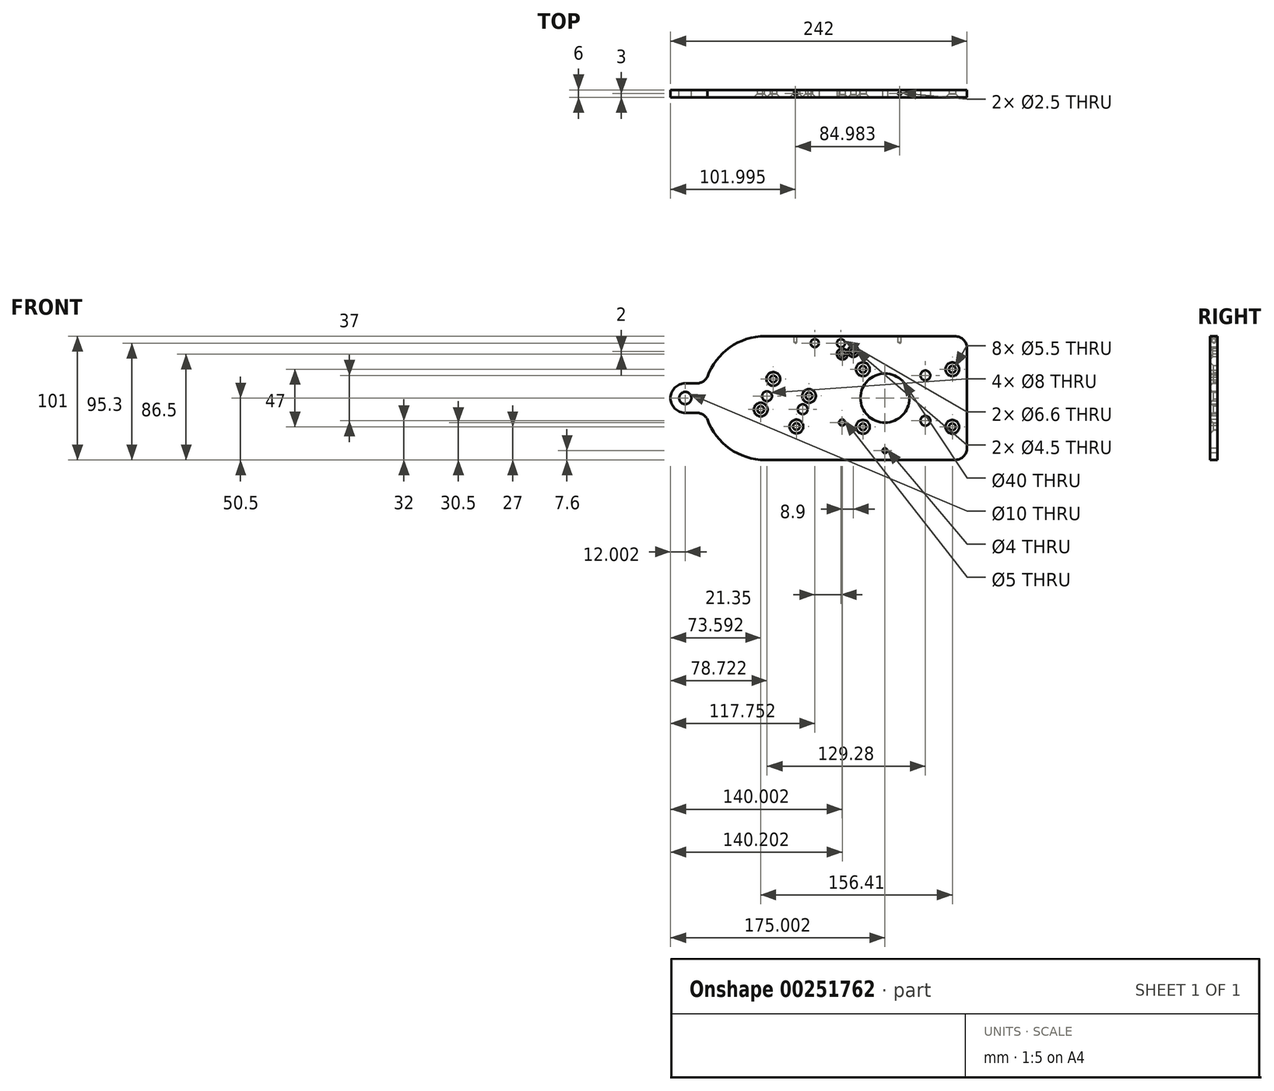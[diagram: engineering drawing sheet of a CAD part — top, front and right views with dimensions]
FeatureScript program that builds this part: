
annotation { "Feature Type Name" : "Feature", "Feature Type Description" : "" }
export const myFeature = defineFeature(function(context is Context, id is Id, definition is map)
    precondition{}
    {
        {
            var Q0;
            Q0=qCreatedBy(makeId("Front.planeOp"),FACE);
            var sketch = newSketch(context, id + "F0", { "sketchPlane" : qUnion([Q0])});
            skCircle(sketch, "E0", {"center": v(37.1, 0) * mm, "radius": 20 * mm});
            skCircle(sketch, "E1", {"center": v(-125.9, 0) * mm, "radius": 5 * mm});
            skArc(sketch, "E2", {"start": v(-125.9, 12) * mm, "mid": v(-137.9, 0) * mm, "end": v(-125.9, -12) * mm});
            skLineSegment(sketch, "E3", {"start": v(-125.9, 12) * mm, "end": v(-116.7, 12) * mm});
            skLineSegment(sketch, "E4", {"start": v(-60.79, 50.5) * mm, "end": v(94.1, 50.5) * mm});
            skLineSegment(sketch, "E5", {"start": v(104.1, 40.5) * mm, "end": v(104.1, -40.5) * mm});
            skLineSegment(sketch, "E6", {"start": v(94.1, -50.5) * mm, "end": v(-29.62, -50.5) * mm});
            skLineSegment(sketch, "E7", {"start": v(-125.9, -12) * mm, "end": v(-116.7, -12) * mm});
            skPoint(sketch, "E8.MirrorCS.start.orphan", {"position": v(-116.7, -12) * mm});
            skPoint(sketch, "E9.visualSharp", {"position": v(-29.62, 50.5) * mm});
            skArc(sketch, "E9.filletArc", {"start": v(-60.79, 50.5) * mm, "mid": v(-60.84, 50.5) * mm, "end": v(-60.89, 50.47) * mm});
            skPoint(sketch, "E10.MirrorCS.end.orphan", {"position": v(-29.62, -50.5) * mm});
            skArc(sketch, "E11", {"start": v(-116.7, 12) * mm, "mid": v(-111.58, 13.41) * mm, "end": v(-107.9, 17.25) * mm});
            skArc(sketch, "E12", {"start": v(-60.79, 50.5) * mm, "mid": v(-89.62, 41.35) * mm, "end": v(-107.9, 17.25) * mm});
            skArc(sketch, "E13.MirrorCS", {"start": v(-116.7, -12) * mm, "mid": v(-111.58, -13.41) * mm, "end": v(-107.9, -17.25) * mm});
            skArc(sketch, "E14.MirrorCS", {"start": v(-60.79, -50.5) * mm, "mid": v(-89.62, -41.35) * mm, "end": v(-107.9, -17.25) * mm});
            skLineSegment(sketch, "E15.MirrorCS", {"start": v(-60.79, -50.5) * mm, "end": v(94.1, -50.5) * mm});
            skPoint(sketch, "E16.visualSharp", {"position": v(104.1, 50.5) * mm});
            skArc(sketch, "E16.filletArc", {"start": v(104.1, 40.5) * mm, "mid": v(101.17, 47.57) * mm, "end": v(94.1, 50.5) * mm});
            skPoint(sketch, "E17.visualSharp", {"position": v(104.1, -50.5) * mm});
            skArc(sketch, "E17.filletArc", {"start": v(94.1, -50.5) * mm, "mid": v(101.17, -47.57) * mm, "end": v(104.1, -40.5) * mm});
            skSolve(sketch);
        }
        {
            var Q0;
            Q0 = qSketchRegion(id + "F0", true);
            extrude(context, id + "F1", {"entities" : qUnion([Q0]), "depth" : 6 * mm});
        }
        {
            var Q0;
            Q0=makeQuery(id+"F1.opExtrude","CAP_FACE",FACE,{"disambiguationData":[OSD([sQuery(id+"F0.wireOp",EDGE,"E0"),sQuery(id+"F0.wireOp",EDGE,"E1"),sQuery(id+"F0.wireOp",EDGE,"E2"),sQuery(id+"F0.wireOp",EDGE,"E3"),sQuery(id+"F0.wireOp",EDGE,"E4"),sQuery(id+"F0.wireOp",EDGE,"E5"),sQuery(id+"F0.wireOp",EDGE,"E7"),sQuery(id+"F0.wireOp",EDGE,"E11"),sQuery(id+"F0.wireOp",EDGE,"E12"),sQuery(id+"F0.wireOp",EDGE,"E13.MirrorCS"),sQuery(id+"F0.wireOp",EDGE,"E14.MirrorCS"),sQuery(id+"F0.wireOp",EDGE,"E15.MirrorCS"),sQuery(id+"F0.wireOp",EDGE,"E16.filletArc"),sQuery(id+"F0.wireOp",EDGE,"E17.filletArc")])],"isStart":false});
            var sketch = newSketch(context, id + "F2", { "sketchPlane" : qUnion([Q0])});
            skPoint(sketch, "E18", {"position": v(-54.05, 15.6) * mm});
            skPoint(sketch, "E19", {"position": v(-64.3, -9.35) * mm});
            skPoint(sketch, "E20", {"position": v(-24.92, 1.75) * mm});
            skPoint(sketch, "E21", {"position": v(-30.05, -9.1) * mm});
            skPoint(sketch, "E22", {"position": v(-35.18, -23.2) * mm});
            skPoint(sketch, "E23", {"position": v(-20.15, 44.8) * mm});
            skPoint(sketch, "E24", {"position": v(1.2, 44.8) * mm});
            skPoint(sketch, "E25", {"position": v(2.3, 36) * mm});
            skPoint(sketch, "E26", {"position": v(11.2, 38) * mm});
            skPoint(sketch, "E27", {"position": v(19.1, 23.5) * mm});
            skPoint(sketch, "E28", {"position": v(19.1, -23.5) * mm});
            skPoint(sketch, "E29", {"position": v(2.1, -20) * mm});
            skPoint(sketch, "E30", {"position": v(37.1, -42.9) * mm});
            skPoint(sketch, "E31", {"position": v(70.1, 18.5) * mm});
            skPoint(sketch, "E32", {"position": v(70.1, -18.5) * mm});
            skPoint(sketch, "E33", {"position": v(37.1, 0) * mm});
            skPoint(sketch, "E34", {"position": v(92.1, 23.5) * mm});
            skPoint(sketch, "E35", {"position": v(92.1, -23.5) * mm});
            skPoint(sketch, "E36", {"position": v(-59.18, 1.52) * mm});
            skSolve(sketch);
        }
        {
            var Q0;
            Q0=sQuery(id+"F2.wireOp",VERTEX,"E24");
            var Q1;
            Q1=sQuery(id+"F2.wireOp",VERTEX,"E23");
            var Q2;
            Q2=makeQuery(id+"F1.opExtrude","SWEPT_BODY",BODY,{"disambiguationData":[OSD([sQuery(id+"F0.wireOp",EDGE,"E0"),sQuery(id+"F0.wireOp",EDGE,"E1"),sQuery(id+"F0.wireOp",EDGE,"E2"),sQuery(id+"F0.wireOp",EDGE,"E3"),sQuery(id+"F0.wireOp",EDGE,"E4"),sQuery(id+"F0.wireOp",EDGE,"E5"),sQuery(id+"F0.wireOp",EDGE,"E7"),sQuery(id+"F0.wireOp",EDGE,"E11"),sQuery(id+"F0.wireOp",EDGE,"E12"),sQuery(id+"F0.wireOp",EDGE,"E13.MirrorCS"),sQuery(id+"F0.wireOp",EDGE,"E14.MirrorCS"),sQuery(id+"F0.wireOp",EDGE,"E15.MirrorCS"),sQuery(id+"F0.wireOp",EDGE,"E16.filletArc"),sQuery(id+"F0.wireOp",EDGE,"E17.filletArc")])]});
            hole(context, id + "F3", {"style" : HoleStyle.SIMPLE, "endStyle" : HoleEndStyle.THROUGH, "standardTappedOrClearance" : lookupTablePath({ "standard" : "ISO", "fit" : "Normal", "size" : "M6", "type" : "Clearance" }), "standardBlindInLast" : lookupTablePath({ "fit" : "Standard", "standard" : "ISO", "size" : "M6", "type" : "Clearance" }), "holeDiameter" : 6.6 * mm, "isTappedThrough" : true, "tappedDepth" : 12 * mm, "tapClearance" : 3, "locations" : qUnion([Q0, Q1]), "scope" : qUnion([Q2])});
        }
        {
            var Q0;
            Q0=sQuery(id+"F2.wireOp",VERTEX,"E25");
            var Q1;
            Q1=sQuery(id+"F2.wireOp",VERTEX,"E26");
            var Q2;
            Q2=makeQuery(id+"F1.opExtrude","SWEPT_BODY",BODY,{"disambiguationData":[OSD([sQuery(id+"F0.wireOp",EDGE,"E0"),sQuery(id+"F0.wireOp",EDGE,"E1"),sQuery(id+"F0.wireOp",EDGE,"E2"),sQuery(id+"F0.wireOp",EDGE,"E3"),sQuery(id+"F0.wireOp",EDGE,"E4"),sQuery(id+"F0.wireOp",EDGE,"E5"),sQuery(id+"F0.wireOp",EDGE,"E7"),sQuery(id+"F0.wireOp",EDGE,"E11"),sQuery(id+"F0.wireOp",EDGE,"E12"),sQuery(id+"F0.wireOp",EDGE,"E13.MirrorCS"),sQuery(id+"F0.wireOp",EDGE,"E14.MirrorCS"),sQuery(id+"F0.wireOp",EDGE,"E15.MirrorCS"),sQuery(id+"F0.wireOp",EDGE,"E16.filletArc"),sQuery(id+"F0.wireOp",EDGE,"E17.filletArc")])]});
            hole(context, id + "F4", {"style" : HoleStyle.C_SINK, "endStyle" : HoleEndStyle.THROUGH, "holeDiameter" : 4.5 * mm, "cSinkDiameter" : 8.96 * mm, "cSinkAngle" : 90 * degree, "isTappedThrough" : true, "tappedDepth" : 12 * mm, "tapClearance" : 3, "locations" : qUnion([Q0, Q1]), "scope" : qUnion([Q2])});
        }
        {
            var Q0;
            Q0=sQuery(id+"F2.wireOp",VERTEX,"E27");
            var Q1;
            Q1=sQuery(id+"F2.wireOp",VERTEX,"E34");
            var Q2;
            Q2=sQuery(id+"F2.wireOp",VERTEX,"E35");
            var Q3;
            Q3=sQuery(id+"F2.wireOp",VERTEX,"E28");
            var Q4;
            Q4=sQuery(id+"F2.wireOp",VERTEX,"E22");
            var Q5;
            Q5=sQuery(id+"F2.wireOp",VERTEX,"E20");
            var Q6;
            Q6=sQuery(id+"F2.wireOp",VERTEX,"E18");
            var Q7;
            Q7=sQuery(id+"F2.wireOp",VERTEX,"E19");
            var Q8;
            Q8=makeQuery(id+"F1.opExtrude","SWEPT_BODY",BODY,{"disambiguationData":[OSD([sQuery(id+"F0.wireOp",EDGE,"E0"),sQuery(id+"F0.wireOp",EDGE,"E1"),sQuery(id+"F0.wireOp",EDGE,"E2"),sQuery(id+"F0.wireOp",EDGE,"E3"),sQuery(id+"F0.wireOp",EDGE,"E4"),sQuery(id+"F0.wireOp",EDGE,"E5"),sQuery(id+"F0.wireOp",EDGE,"E7"),sQuery(id+"F0.wireOp",EDGE,"E11"),sQuery(id+"F0.wireOp",EDGE,"E12"),sQuery(id+"F0.wireOp",EDGE,"E13.MirrorCS"),sQuery(id+"F0.wireOp",EDGE,"E14.MirrorCS"),sQuery(id+"F0.wireOp",EDGE,"E15.MirrorCS"),sQuery(id+"F0.wireOp",EDGE,"E16.filletArc"),sQuery(id+"F0.wireOp",EDGE,"E17.filletArc")])]});
            hole(context, id + "F5", {"style" : HoleStyle.C_SINK, "endStyle" : HoleEndStyle.THROUGH, "holeDiameter" : 5.5 * mm, "cSinkDiameter" : 11.2 * mm, "cSinkAngle" : 90 * degree, "isTappedThrough" : true, "tappedDepth" : 12 * mm, "tapClearance" : 3, "locations" : qUnion([Q0, Q1, Q2, Q3, Q4, Q5, Q6, Q7]), "scope" : qUnion([Q8])});
        }
        {
            var Q0;
            Q0=sQuery(id+"F2.wireOp",VERTEX,"E30");
            var Q1;
            Q1=makeQuery(id+"F1.opExtrude","SWEPT_BODY",BODY,{"disambiguationData":[OSD([sQuery(id+"F0.wireOp",EDGE,"E0"),sQuery(id+"F0.wireOp",EDGE,"E1"),sQuery(id+"F0.wireOp",EDGE,"E2"),sQuery(id+"F0.wireOp",EDGE,"E3"),sQuery(id+"F0.wireOp",EDGE,"E4"),sQuery(id+"F0.wireOp",EDGE,"E5"),sQuery(id+"F0.wireOp",EDGE,"E7"),sQuery(id+"F0.wireOp",EDGE,"E11"),sQuery(id+"F0.wireOp",EDGE,"E12"),sQuery(id+"F0.wireOp",EDGE,"E13.MirrorCS"),sQuery(id+"F0.wireOp",EDGE,"E14.MirrorCS"),sQuery(id+"F0.wireOp",EDGE,"E15.MirrorCS"),sQuery(id+"F0.wireOp",EDGE,"E16.filletArc"),sQuery(id+"F0.wireOp",EDGE,"E17.filletArc")])]});
            hole(context, id + "F6", {"style" : HoleStyle.SIMPLE, "endStyle" : HoleEndStyle.THROUGH, "holeDiameter" : 4 * mm, "isTappedThrough" : true, "tappedDepth" : 12 * mm, "tapClearance" : 3, "locations" : qUnion([Q0]), "scope" : qUnion([Q1])});
        }
        {
            var Q0;
            Q0=sQuery(id+"F2.wireOp",VERTEX,"E31");
            var Q1;
            Q1=sQuery(id+"F2.wireOp",VERTEX,"E32");
            var Q2;
            Q2=sQuery(id+"F2.wireOp",VERTEX,"E21");
            var Q3;
            Q3=sQuery(id+"F2.wireOp",VERTEX,"E36");
            var Q4;
            Q4=makeQuery(id+"F1.opExtrude","SWEPT_BODY",BODY,{"disambiguationData":[OSD([sQuery(id+"F0.wireOp",EDGE,"E0"),sQuery(id+"F0.wireOp",EDGE,"E1"),sQuery(id+"F0.wireOp",EDGE,"E2"),sQuery(id+"F0.wireOp",EDGE,"E3"),sQuery(id+"F0.wireOp",EDGE,"E4"),sQuery(id+"F0.wireOp",EDGE,"E5"),sQuery(id+"F0.wireOp",EDGE,"E7"),sQuery(id+"F0.wireOp",EDGE,"E11"),sQuery(id+"F0.wireOp",EDGE,"E12"),sQuery(id+"F0.wireOp",EDGE,"E13.MirrorCS"),sQuery(id+"F0.wireOp",EDGE,"E14.MirrorCS"),sQuery(id+"F0.wireOp",EDGE,"E15.MirrorCS"),sQuery(id+"F0.wireOp",EDGE,"E16.filletArc"),sQuery(id+"F0.wireOp",EDGE,"E17.filletArc")])]});
            hole(context, id + "F7", {"style" : HoleStyle.SIMPLE, "endStyle" : HoleEndStyle.THROUGH, "holeDiameter" : 8 * mm, "isTappedThrough" : true, "tappedDepth" : 12 * mm, "tapClearance" : 3, "locations" : qUnion([Q0, Q1, Q2, Q3]), "scope" : qUnion([Q4])});
        }
        {
            var Q0;
            Q0=sQuery(id+"F2.wireOp",VERTEX,"E29");
            var Q1;
            Q1=makeQuery(id+"F1.opExtrude","SWEPT_BODY",BODY,{"disambiguationData":[OSD([sQuery(id+"F0.wireOp",EDGE,"E0"),sQuery(id+"F0.wireOp",EDGE,"E1"),sQuery(id+"F0.wireOp",EDGE,"E2"),sQuery(id+"F0.wireOp",EDGE,"E3"),sQuery(id+"F0.wireOp",EDGE,"E4"),sQuery(id+"F0.wireOp",EDGE,"E5"),sQuery(id+"F0.wireOp",EDGE,"E7"),sQuery(id+"F0.wireOp",EDGE,"E11"),sQuery(id+"F0.wireOp",EDGE,"E12"),sQuery(id+"F0.wireOp",EDGE,"E13.MirrorCS"),sQuery(id+"F0.wireOp",EDGE,"E14.MirrorCS"),sQuery(id+"F0.wireOp",EDGE,"E15.MirrorCS"),sQuery(id+"F0.wireOp",EDGE,"E16.filletArc"),sQuery(id+"F0.wireOp",EDGE,"E17.filletArc")])]});
            hole(context, id + "F8", {"style" : HoleStyle.SIMPLE, "endStyle" : HoleEndStyle.THROUGH, "holeDiameter" : 5 * mm, "isTappedThrough" : true, "tappedDepth" : 12 * mm, "tapClearance" : 3, "locations" : qUnion([Q0]), "scope" : qUnion([Q1])});
        }
        {
            var Q0;
            Q0=makeQuery(id+"F1.opExtrude","SWEPT_FACE",FACE,{"disambiguationData":[OSD([sQuery(id+"F0.wireOp",EDGE,"E4")])]});
            var sketch = newSketch(context, id + "F9", { "sketchPlane" : qUnion([Q0])});
            skPoint(sketch, "E37", {"position": v(-35.9, -3) * mm});
            skPoint(sketch, "E38", {"position": v(49.08, -3) * mm});
            skSolve(sketch);
        }
        {
            var Q0;
            Q0=sQuery(id+"F9.wireOp",VERTEX,"E38");
            var Q1;
            Q1=sQuery(id+"F9.wireOp",VERTEX,"E37");
            var Q2;
            Q2=makeQuery(id+"F1.opExtrude","SWEPT_BODY",BODY,{"disambiguationData":[OSD([sQuery(id+"F0.wireOp",EDGE,"E0"),sQuery(id+"F0.wireOp",EDGE,"E1"),sQuery(id+"F0.wireOp",EDGE,"E2"),sQuery(id+"F0.wireOp",EDGE,"E3"),sQuery(id+"F0.wireOp",EDGE,"E4"),sQuery(id+"F0.wireOp",EDGE,"E5"),sQuery(id+"F0.wireOp",EDGE,"E7"),sQuery(id+"F0.wireOp",EDGE,"E11"),sQuery(id+"F0.wireOp",EDGE,"E12"),sQuery(id+"F0.wireOp",EDGE,"E13.MirrorCS"),sQuery(id+"F0.wireOp",EDGE,"E14.MirrorCS"),sQuery(id+"F0.wireOp",EDGE,"E15.MirrorCS"),sQuery(id+"F0.wireOp",EDGE,"E16.filletArc"),sQuery(id+"F0.wireOp",EDGE,"E17.filletArc")])]});
            hole(context, id + "F10", {"style" : HoleStyle.SIMPLE, "endStyle" : HoleEndStyle.BLIND, "holeDiameter" : 2.5 * mm, "holeDepth" : 5 * mm, "isTappedThrough" : true, "tappedDepth" : 12 * mm, "tapClearance" : 3, "locations" : qUnion([Q0, Q1]), "scope" : qUnion([Q2])});
        }
    });
